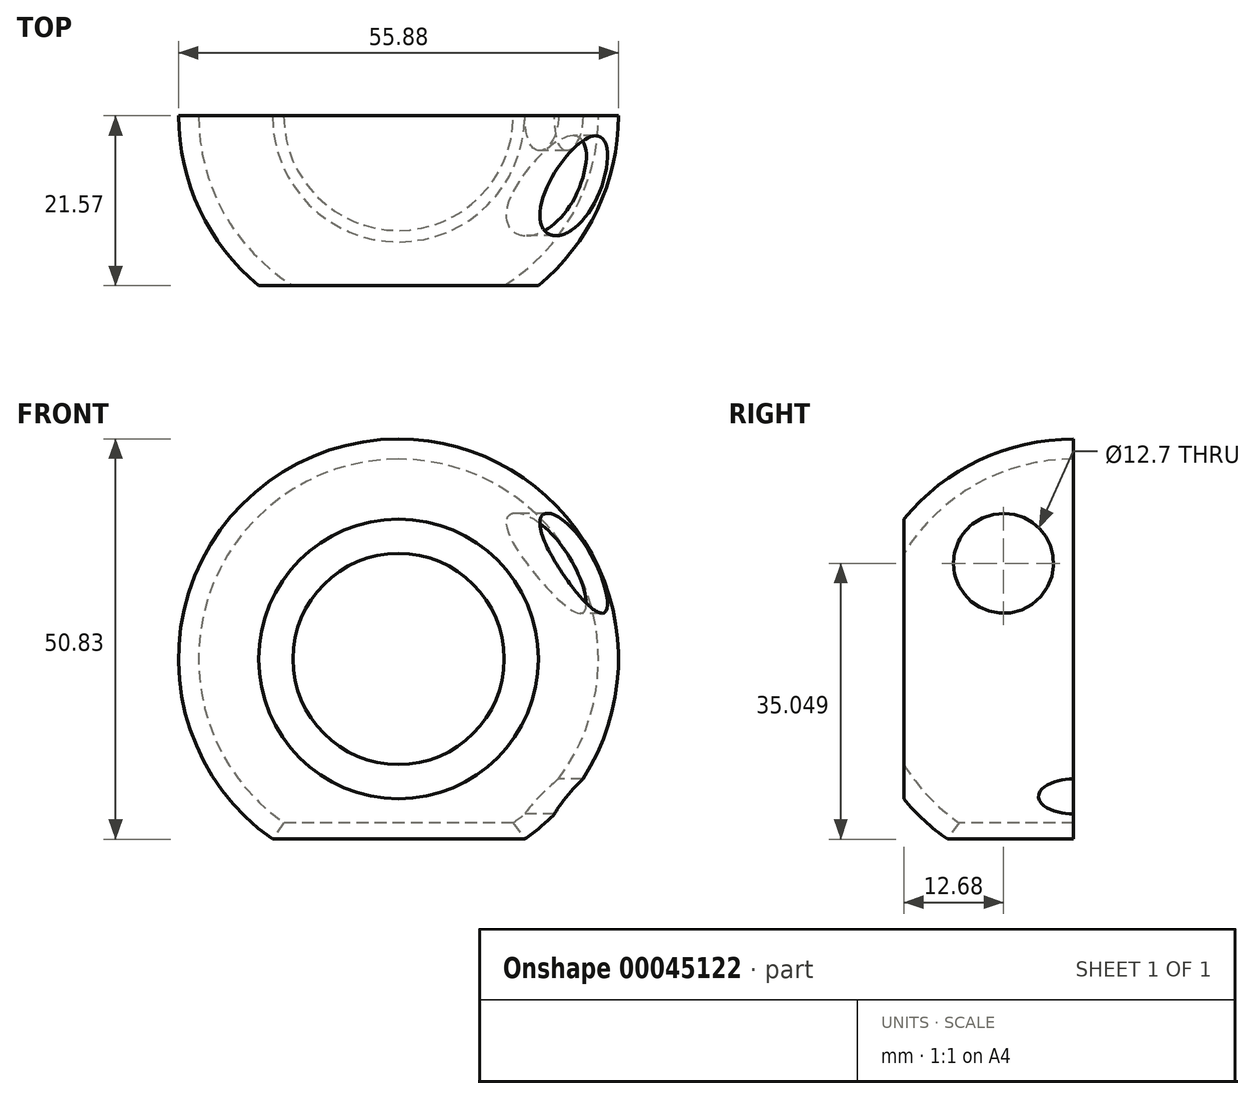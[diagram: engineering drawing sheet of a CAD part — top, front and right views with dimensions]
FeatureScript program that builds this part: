
annotation { "Feature Type Name" : "Feature", "Feature Type Description" : "" }
export const myFeature = defineFeature(function(context is Context, id is Id, definition is map)
    precondition{}
    {
        {
            var Q0;
            Q0=qCreatedBy(makeId("Front.planeOp"),FACE);
            var sketch = newSketch(context, id + "F0", { "sketchPlane" : qUnion([Q0])});
            skLineSegment(sketch, "E0", {"start": v(0, 0) * mm, "end": v(0, 25.4) * mm});
            skLineSegment(sketch, "E1", {"start": v(0, 0) * mm, "end": v(0, -25.4) * mm});
            skArc(sketch, "E2", {"start": v(0, 25.4) * mm, "mid": v(-25.4, 0) * mm, "end": v(0, -25.4) * mm});
            skLineSegment(sketch, "E3", {"start": v(0, 25.4) * mm, "end": v(0, 27.94) * mm});
            skLineSegment(sketch, "E4", {"start": v(0, -25.4) * mm, "end": v(0, -27.94) * mm});
            skLineSegment(sketch, "E5", {"start": v(-25.4, 0) * mm, "end": v(-27.94, 0) * mm});
            skPoint(sketch, "E5.endSnap0", {"position": v(-25.4, 0) * mm});
            skArc(sketch, "E6", {"start": v(0, 27.94) * mm, "mid": v(-27.94, 0) * mm, "end": v(0, -27.94) * mm});
            skLineSegment(sketch, "E7", {"start": v(-25.4, 0) * mm, "end": v(-20.32, 0) * mm});
            skLineSegment(sketch, "E8", {"start": v(0, 0) * mm, "end": v(-16.03, -22.89) * mm});
            skSolve(sketch);
        }
        {
            var Q0;
            {var subQ5=sQuery(id+"F0.wireOp",EDGE,"E5");Q0=makeQuery(id+"F0.imprint","IMPRINT",FACE,{"disambiguationData":[TD([[makeQuery(id+"F0.imprint","IMPRINT",EDGE,{"derivedFrom":subQ5}),1.0]])]});}
            var Q1;
            {var subQ2=sQuery(id+"F0.wireOp",EDGE,"E3");Q1=makeQuery(id+"F0.imprint","IMPRINT",FACE,{"disambiguationData":[TD([[makeQuery(id+"F0.imprint","IMPRINT",EDGE,{"derivedFrom":subQ2}),1.0]])]});}
            var Q2;
            Q2=sQuery(id+"F0.wireOp",EDGE,"E0");
            revolve(context, id + "F1", {"entities" : qUnion([Q0, Q1]), "axis" : qUnion([Q2]), "revolveType" : RevolveType.ONE_DIRECTION, "angle" : 180 * degree});
        }
        {
            var Q0;
            Q0=qCreatedBy(makeId("Right.planeOp"),FACE);
            var sketch = newSketch(context, id + "F2", { "sketchPlane" : qUnion([Q0])});
            skLineSegment(sketch, "E9", {"start": v(0, 0) * mm, "end": v(0, -15.24) * mm});
            skLineSegment(sketch, "E10", {"start": v(0, -15.24) * mm, "end": v(0, -19.69) * mm});
            skEllipse(sketch, "E11", {"center": v(0, -17.46) * mm, "majorRadius": 4.45 * mm, "minorRadius": 2.22 * mm, "majorAxis": v(1, 0)});
            skLineSegment(sketch, "E12", {"start": v(0, 0) * mm, "end": v(0, 12.16) * mm});
            skLineSegment(sketch, "E13", {"start": v(0, 12.16) * mm, "end": v(-8.9, 12.16) * mm});
            skCircle(sketch, "E14", {"center": v(-8.9, 12.16) * mm, "radius": 6.35 * mm});
            skLineSegment(sketch, "E15", {"start": v(0, 0) * mm, "end": v(-21.6, 0) * mm});
            skLineSegment(sketch, "E16", {"start": v(-21.6, 0) * mm, "end": v(-27.94, 0) * mm});
            skLineSegment(sketch, "E17.rect.bottom", {"start": v(-21.57, 17.98) * mm, "end": v(-27.96, 17.98) * mm});
            skLineSegment(sketch, "E17.rect.top", {"start": v(-21.57, -17.98) * mm, "end": v(-27.96, -17.98) * mm});
            skLineSegment(sketch, "E17.rect.left", {"start": v(-21.57, 17.98) * mm, "end": v(-21.57, -17.98) * mm});
            skLineSegment(sketch, "E17.rect.right", {"start": v(-27.96, 17.98) * mm, "end": v(-27.96, -17.98) * mm});
            skPoint(sketch, "E17.rect.middle", {"position": v(-24.77, 0) * mm});
            skSolve(sketch);
        }
        {
            var Q0;
            Q0=makeQuery(id+"F2.imprint","IMPRINT",FACE,{"disambiguationData":[TD([[makeQuery(id+"F2.imprint","IMPRINT",EDGE,{"derivedFrom":sQuery(id+"F2.wireOp",EDGE,"E14")}),1.0]])]});
            var Q1;
            {var subQ1=sQuery(id+"F2.wireOp",EDGE,"E10");Q1=makeQuery(id+"F2.imprint","IMPRINT",FACE,{"disambiguationData":[TD([[makeQuery(id+"F2.imprint","IMPRINT",EDGE,{"derivedFrom":subQ1}),-1.0]])]});}
            var Q2;
            {var subQ0=sQuery(id+"F2.wireOp",EDGE,"E17.rect.bottom");Q2=makeQuery(id+"F2.imprint","IMPRINT",FACE,{"disambiguationData":[TD([[makeQuery(id+"F2.imprint","IMPRINT",EDGE,{"derivedFrom":subQ0}),1.0]])]});}
            extrude(context, id + "F3", {"entities" : qUnion([Q0, Q1, Q2]), "operationType" : NewBodyOperationType.REMOVE, "depth" : 107.6 * mm});
        }
        {
            var Q0;
            {var subQ0=sQuery(id+"F2.wireOp",EDGE,"E17.rect.bottom");Q0=makeQuery(id+"F2.imprint","IMPRINT",FACE,{"disambiguationData":[TD([[makeQuery(id+"F2.imprint","IMPRINT",EDGE,{"derivedFrom":subQ0}),1.0]])]});}
            extrude(context, id + "F4", {"entities" : qUnion([Q0]), "operationType" : NewBodyOperationType.REMOVE, "oppositeDirection" : true, "depth" : 25.4 * mm});
        }
    });
